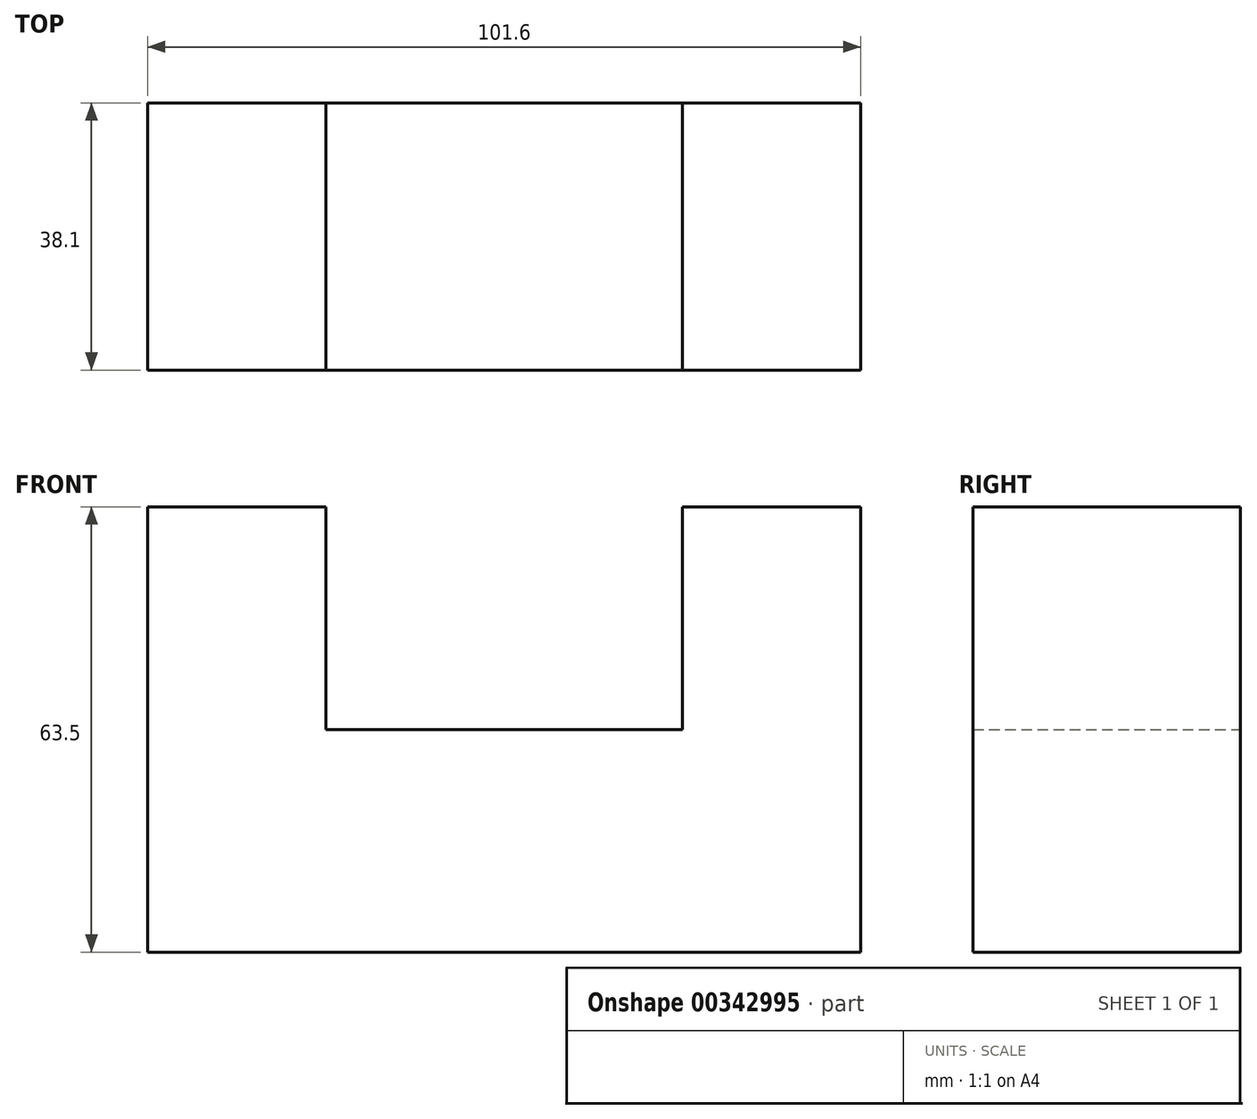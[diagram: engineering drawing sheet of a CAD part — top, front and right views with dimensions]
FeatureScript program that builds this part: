
annotation { "Feature Type Name" : "Feature", "Feature Type Description" : "" }
export const myFeature = defineFeature(function(context is Context, id is Id, definition is map)
    precondition{}
    {
        {
            var Q0;
            Q0=qCreatedBy(makeId("Front.planeOp"),FACE);
            var sketch = newSketch(context, id + "F0", { "sketchPlane" : qUnion([Q0])});
            skLineSegment(sketch, "E0", {"start": v(-50.8, -38.91) * mm, "end": v(50.8, -38.91) * mm});
            skLineSegment(sketch, "E1", {"start": v(50.8, -38.91) * mm, "end": v(50.8, 24.59) * mm});
            skLineSegment(sketch, "E2", {"start": v(-50.8, -38.91) * mm, "end": v(-50.8, 24.59) * mm});
            skLineSegment(sketch, "E3", {"start": v(-50.8, 24.59) * mm, "end": v(-25.4, 24.59) * mm});
            skLineSegment(sketch, "E4", {"start": v(50.8, 24.59) * mm, "end": v(25.4, 24.59) * mm});
            skLineSegment(sketch, "E5", {"start": v(-25.4, 24.59) * mm, "end": v(-25.4, -7.16) * mm});
            skLineSegment(sketch, "E6", {"start": v(25.4, 24.59) * mm, "end": v(25.4, -7.16) * mm});
            skLineSegment(sketch, "E7", {"start": v(-25.4, -7.16) * mm, "end": v(25.4, -7.16) * mm});
            skSolve(sketch);
        }
        {
            var Q0;
            Q0=makeQuery(id+"F0.imprint","IMPRINT",FACE,{"disambiguationData":[TD([[makeQuery(id+"F0.imprint","IMPRINT",EDGE,{"derivedFrom":sQuery(id+"F0.wireOp",EDGE,"E0")}),1.0]])]});
            extrude(context, id + "F1", {"entities" : qUnion([Q0]), "depth" : 38.1 * mm});
        }
    });
